# Revit family: Bolton Chairs
name_source: partatom
category: Furniture
units: mm (PartAtom-declared; Revit-internal decimal feet)

## family parameters
Always vertical = Yes
Cut with Voids When Loaded = No
OmniClass Number = 23.40.20.00
OmniClass Title = General Furniture and Specialties
Room Calculation Point = No
Shared = No
Work Plane-Based = No

## types (16) — shared parameters
Default Elevation = 0' - 0"
Manufacturer = AIS Inc
Product = BOLTON CHAIRS
URL = https://www.ais-inc.com

## per-type parameters (varying)
| type | 4400C-1D Arm | 4400C-3D Arm | 4400C-4D Arm | 4400C-No Arm | Description | Model |
| 4400C-1D Arms | Yes | No | No | No | Configurable High-Back Task Chair with 1D Arms | 4400C |
| 4400C-3D Arms | No | Yes | No | No | Configurable High-Back Task Chair with 3D Arms | 4400C |
| 4400C-4D Arms | No | No | Yes | No | Configurable High-Back Task Chair with 4D Arms | 4400C |
| 4400C-No Arms | No | No | No | Yes | Configurable High-Back Task Chair with No Arms | 4400C |
| 4430C-1D Arms | No | No | No | No | Configurable High-Back Task Chair with 1D Arms | 4430C |
| 4430C-3D Arms | No | No | No | No | Configurable High-Back Task Chair with 3D Arms | 4430C |
| 4430C-4D Arms | No | No | No | No | Configurable High-Back Task Chair with 4D Arms | 4430C |
| 4430C-No Arms | No | No | No | No | Configurable High-Back Task Chair with No Arms | 4430C |
| 4471C-1D Arms | No | No | No | No | Configurable Mid-Back Task Chair with 1D Arms | 4471C |
| 4471C-3D Arms | No | No | No | No | Configurable Mid-Back Task Chair with 3D Arms | 4471C |
| 4471C-4D Arms | No | No | No | No | Configurable Mid-Back Task Chair with 4D Arms | 4471C |
| 4471C-No Arms | No | No | No | No | Configurable Mid-Back Task Chair with No Arms | 4471C |
| 4481C-1D Arms | No | No | No | No | Configurable Mid-Back Task Chair with 1D Arms | 4481C |
| 4481C-3D Arms | No | No | No | No | Configurable Mid-Back Task Chair with 3D Arms | 4481C |
| 4481C-4D Arms | No | No | No | No | Configurable Mid-Back Task Chair with 4D Arms | 4481C |
| 4481C-No Arms | No | No | No | No | Configurable Mid-Back Task Chair with No Arms | 4481C |

type visibility flags (boolean, named after types; folded from table):
- 4400C-1D Arms: Yes: (none)
- 4400C-3D Arms: Yes: (none)
- 4400C-4D Arms: Yes: (none)
- 4400C-No Arms: Yes: (none)
- 4430C-1D Arms: Yes: 4430C-1D Arms
- 4430C-3D Arms: Yes: 4430C-3D Arms
- 4430C-4D Arms: Yes: 4430C-4D Arms
- 4430C-No Arms: Yes: 4430C-No Arms
- 4471C-1D Arms: Yes: 4471C-1D Arms
- 4471C-3D Arms: Yes: 4471C-3D Arms
- 4471C-4D Arms: Yes: 4471C-4D Arms
- 4471C-No Arms: Yes: 4471C-No Arms
- 4481C-1D Arms: Yes: 4481C-1D Arms
- 4481C-3D Arms: Yes: 4481C-3D Arms
- 4481C-4D Arms: Yes: 4481C-4D Arms
- 4481C-No Arms: Yes: 4481C-No Arms

## geometry (parser evidence)
native form markers: Sweep x3
no freeform markers — native parametric forms only
